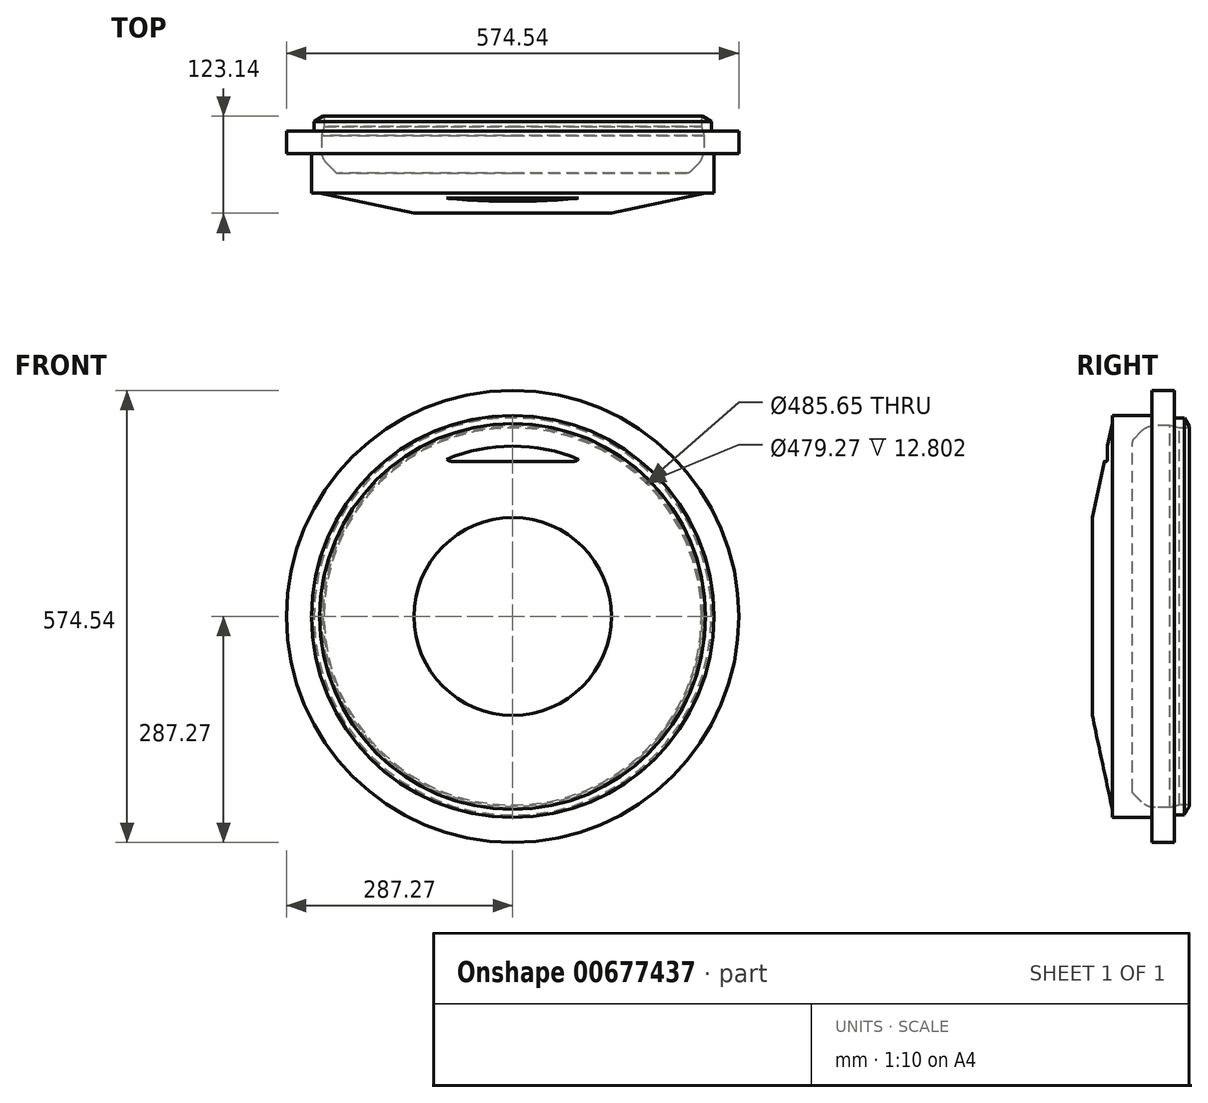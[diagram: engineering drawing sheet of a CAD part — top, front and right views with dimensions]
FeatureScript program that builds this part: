
annotation { "Feature Type Name" : "Feature", "Feature Type Description" : "" }
export const myFeature = defineFeature(function(context is Context, id is Id, definition is map)
    precondition{}
    {
        {
            var Q0;
            Q0=qCreatedBy(makeId("Right.planeOp"),FACE);
            var sketch = newSketch(context, id + "F0", { "sketchPlane" : qUnion([Q0])});
            skLineSegment(sketch, "E0", {"start": v(0, 0) * mm, "end": v(123.14, 0) * mm, "construction": true});
            skLineSegment(sketch, "E1", {"start": v(116.68, 252.35) * mm, "end": v(104.47, 252.35) * mm});
            skLineSegment(sketch, "E2.0", {"start": v(75.9, 287.27) * mm, "end": v(104.47, 287.27) * mm});
            skLineSegment(sketch, "E3", {"start": v(104.47, 252.35) * mm, "end": v(104.47, 287.27) * mm});
            skLineSegment(sketch, "E4.0", {"start": v(75.9, 255.52) * mm, "end": v(75.9, 287.27) * mm});
            skLineSegment(sketch, "E5.0", {"start": v(25.4, 245.03) * mm, "end": v(25.4, 255.52) * mm});
            skLineSegment(sketch, "E6", {"start": v(0, 0) * mm, "end": v(0, 125.48) * mm});
            skLineSegment(sketch, "E7.0", {"start": v(25.4, 255.52) * mm, "end": v(75.9, 255.52) * mm});
            skLineSegment(sketch, "E8", {"start": v(0, 125.48) * mm, "end": v(25.4, 245.03) * mm});
            skLineSegment(sketch, "E9", {"start": v(123.14, 239.64) * mm, "end": v(110.34, 239.64) * mm});
            skLineSegment(sketch, "E10", {"start": v(110.34, 239.64) * mm, "end": v(98.44, 242.82) * mm});
            skArc(sketch, "E11", {"start": v(80.4, 242.82) * mm, "mid": v(70.67, 240.9) * mm, "end": v(62.43, 235.38) * mm});
            skLineSegment(sketch, "E12.0", {"start": v(50.8, 0) * mm, "end": v(50.8, 221.12) * mm});
            skLineSegment(sketch, "E13", {"start": v(52.66, 225.61) * mm, "end": v(62.43, 235.38) * mm});
            skArc(sketch, "E14.filletArc", {"start": v(52.66, 225.61) * mm, "mid": v(51.28, 223.55) * mm, "end": v(50.8, 221.12) * mm});
            skLineSegment(sketch, "E15.trimOffspring", {"start": v(80.4, 242.82) * mm, "end": v(98.44, 242.82) * mm});
            skLineSegment(sketch, "E16", {"start": v(123.14, 239.64) * mm, "end": v(123.14, 241.16) * mm});
            skLineSegment(sketch, "E17", {"start": v(123.14, 241.16) * mm, "end": v(116.68, 252.35) * mm});
            skLineSegment(sketch, "E18", {"start": v(0, 0) * mm, "end": v(50.8, 0) * mm});
            skSolve(sketch);
        }
        {
            var Q0;
            Q0 = qSketchRegion(id + "F0", true);
            var Q1;
            Q1=sQuery(id+"F0.wireOp",EDGE,"E0");
            revolve(context, id + "F1", {"entities" : qUnion([Q0]), "axis" : qUnion([Q1]), "revolveType" : RevolveType.FULL});
        }
        {
            var Q0;
            Q0=makeQuery(id+"F1.opRevolve","SWEPT_FACE",FACE,{"disambiguationData":[OSD([sQuery(id+"F0.wireOp",EDGE,"E12.0")])]});
            cPlane(context, id + "F2", {"entities" : qUnion([Q0]), "cplaneType" : CPlaneType.OFFSET, "offset" : 31.47 * mm, "oppositeDirection" : true, "width" : 152.4 * mm, "height" : 152.4 * mm});
        }
        {
            var Q0;
            Q0=qCreatedBy(id+"F2.planeOp",FACE);
            var sketch = newSketch(context, id + "F3", { "sketchPlane" : qUnion([Q0])});
            skLineSegment(sketch, "E19", {"start": v(0, 0) * mm, "end": v(77.18, 0) * mm, "construction": true});
            skLineSegment(sketch, "E20", {"start": v(0, 0) * mm, "end": v(-77.18, 0) * mm, "construction": true});
            skLineSegment(sketch, "E21.0", {"start": v(0, 207.06) * mm, "end": v(77.18, 207.06) * mm, "construction": true});
            skLineSegment(sketch, "E21.1", {"start": v(0, 207.06) * mm, "end": v(-77.18, 207.06) * mm, "construction": true});
            skArc(sketch, "E22", {"start": v(77.18, 197.12) * mm, "mid": v(87.12, 207.06) * mm, "end": v(77.18, 217) * mm});
            skArc(sketch, "E23", {"start": v(-77.18, 217) * mm, "mid": v(-87.12, 207.06) * mm, "end": v(-77.18, 197.12) * mm});
            skLineSegment(sketch, "E24.0", {"start": v(-77.18, 217) * mm, "end": v(77.18, 217) * mm});
            skLineSegment(sketch, "E25.0", {"start": v(-77.18, 197.12) * mm, "end": v(77.18, 197.12) * mm});
            skSolve(sketch);
        }
        {
            var Q0;
            Q0 = qSketchRegion(id + "F3", true);
            extrude(context, id + "F4", {"entities" : qUnion([Q0]), "operationType" : NewBodyOperationType.REMOVE, "endBound" : BoundingType.THROUGH_ALL, "oppositeDirection" : true, "depth" : 25.4 * mm, "offsetDistance" : 25.4 * mm});
        }
    });
